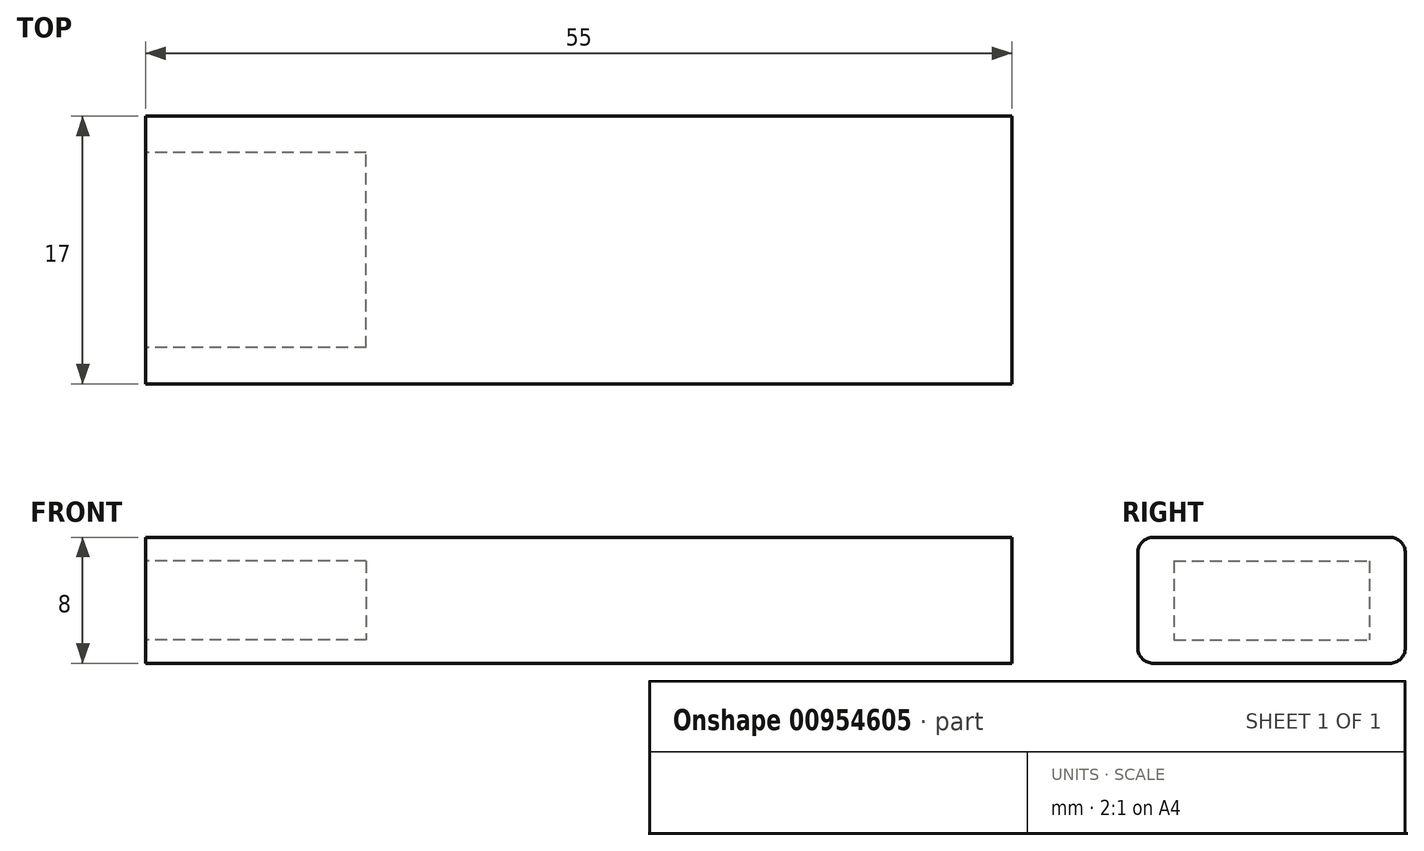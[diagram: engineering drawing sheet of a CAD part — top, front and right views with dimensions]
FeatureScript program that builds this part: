
annotation { "Feature Type Name" : "Feature", "Feature Type Description" : "" }
export const myFeature = defineFeature(function(context is Context, id is Id, definition is map)
    precondition{}
    {
        {
            var Q0;
            Q0=qCreatedBy(makeId("Front.planeOp"),FACE);
            var sketch = newSketch(context, id + "F0", { "sketchPlane" : qUnion([Q0])});
            skLineSegment(sketch, "E0.bottom", {"start": v(7.5, 4) * mm, "end": v(-7.5, 4) * mm});
            skLineSegment(sketch, "E0.top", {"start": v(7.5, -4) * mm, "end": v(-7.5, -4) * mm});
            skLineSegment(sketch, "E0.left", {"start": v(8.5, 3) * mm, "end": v(8.5, -3) * mm});
            skLineSegment(sketch, "E0.right", {"start": v(-8.5, 3) * mm, "end": v(-8.5, -3) * mm});
            skPoint(sketch, "E0.middle", {"position": v(0, 0) * mm});
            skPoint(sketch, "E1.visualSharp", {"position": v(-8.5, 4) * mm});
            skArc(sketch, "E1.filletArc", {"start": v(-7.5, 4) * mm, "mid": v(-8.2, 3.7) * mm, "end": v(-8.5, 3) * mm});
            skPoint(sketch, "E2.visualSharp", {"position": v(8.5, 4) * mm});
            skArc(sketch, "E2.filletArc", {"start": v(8.5, 3) * mm, "mid": v(8.2, 3.7) * mm, "end": v(7.5, 4) * mm});
            skPoint(sketch, "E3.visualSharp", {"position": v(8.5, -4) * mm});
            skArc(sketch, "E3.filletArc", {"start": v(7.5, -4) * mm, "mid": v(8.2, -3.7) * mm, "end": v(8.5, -3) * mm});
            skPoint(sketch, "E4.visualSharp", {"position": v(-8.5, -4) * mm});
            skArc(sketch, "E4.filletArc", {"start": v(-8.5, -3) * mm, "mid": v(-8.2, -3.7) * mm, "end": v(-7.5, -4) * mm});
            skSolve(sketch);
        }
        {
            var Q0;
            Q0 = qSketchRegion(id + "F0", true);
            extrude(context, id + "F1", {"entities" : qUnion([Q0]), "depth" : 55 * mm, "offsetDistance" : 25 * mm});
        }
        {
            var Q0;
            Q0=makeQuery(id+"F1.opExtrude","CAP_FACE",FACE,{"disambiguationData":[OSD([sQuery(id+"F0.wireOp",EDGE,"E0.bottom"),sQuery(id+"F0.wireOp",EDGE,"E0.top"),sQuery(id+"F0.wireOp",EDGE,"E0.left"),sQuery(id+"F0.wireOp",EDGE,"E0.right"),sQuery(id+"F0.wireOp",EDGE,"E1.filletArc"),sQuery(id+"F0.wireOp",EDGE,"E2.filletArc"),sQuery(id+"F0.wireOp",EDGE,"E3.filletArc"),sQuery(id+"F0.wireOp",EDGE,"E4.filletArc")])],"isStart":false});
            var sketch = newSketch(context, id + "F2", { "sketchPlane" : qUnion([Q0])});
            skLineSegment(sketch, "E5.bottom", {"start": v(6.2, 2.5) * mm, "end": v(-6.2, 2.5) * mm});
            skLineSegment(sketch, "E5.top", {"start": v(6.2, -2.5) * mm, "end": v(-6.2, -2.5) * mm});
            skLineSegment(sketch, "E5.left", {"start": v(6.2, 2.5) * mm, "end": v(6.2, -2.5) * mm});
            skLineSegment(sketch, "E5.right", {"start": v(-6.2, 2.5) * mm, "end": v(-6.2, -2.5) * mm});
            skPoint(sketch, "E5.middle", {"position": v(0, 0) * mm});
            skSolve(sketch);
        }
        {
            var Q0;
            Q0 = qSketchRegion(id + "F2", true);
            extrude(context, id + "F3", {"entities" : qUnion([Q0]), "operationType" : NewBodyOperationType.REMOVE, "oppositeDirection" : true, "depth" : 14 * mm, "offsetDistance" : 25 * mm});
        }
        {
            var Q0;
            Q0=makeQuery(id+"F1.opExtrude","SWEPT_BODY",BODY,{"disambiguationData":[OSD([sQuery(id+"F0.wireOp",EDGE,"E0.bottom"),sQuery(id+"F0.wireOp",EDGE,"E0.top"),sQuery(id+"F0.wireOp",EDGE,"E0.left"),sQuery(id+"F0.wireOp",EDGE,"E0.right"),sQuery(id+"F0.wireOp",EDGE,"E1.filletArc"),sQuery(id+"F0.wireOp",EDGE,"E2.filletArc"),sQuery(id+"F0.wireOp",EDGE,"E3.filletArc"),sQuery(id+"F0.wireOp",EDGE,"E4.filletArc")])]});
            var Q1;
            Q1=makeQuery(id+"F1.opExtrude","CAP_EDGE",EDGE,{"disambiguationData":[OSD([sQuery(id+"F0.wireOp",EDGE,"E0.right")])],"isStart":true});
            transform(context, id + "F4", {"entities" : qUnion([Q0]), "transformType" : TransformType.ROTATION, "transformAxis" : qUnion([Q1]), "angle" : 90 * degree, "makeCopy" : false});
        }
    });
